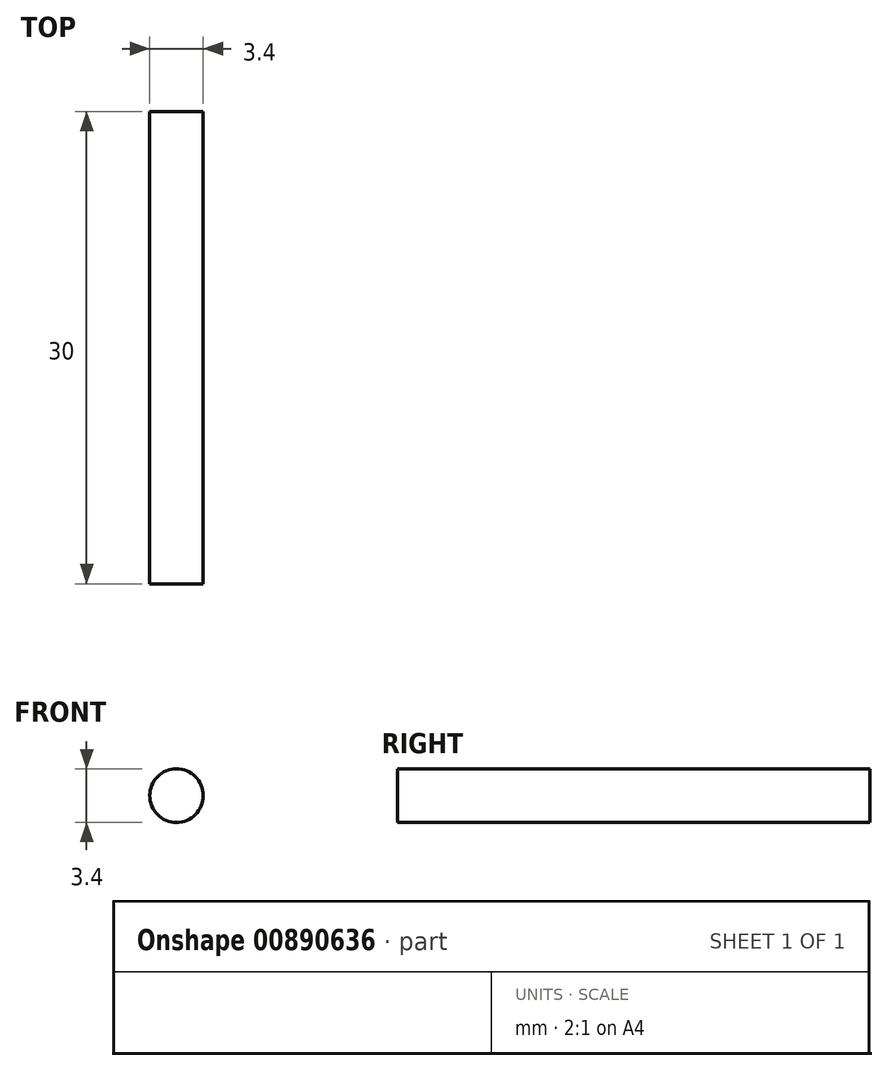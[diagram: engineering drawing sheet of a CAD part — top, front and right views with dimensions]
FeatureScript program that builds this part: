
annotation { "Feature Type Name" : "Feature", "Feature Type Description" : "" }
export const myFeature = defineFeature(function(context is Context, id is Id, definition is map)
    precondition{}
    {
        {
            var Q0;
            Q0=qCreatedBy(makeId("Front.planeOp"),FACE);
            var sketch = newSketch(context, id + "F0", { "sketchPlane" : qUnion([Q0])});
            skCircle(sketch, "E0", {"center": v(0, 0) * mm, "radius": 1.7 * mm});
            skSolve(sketch);
        }
        {
            var Q0;
            Q0=makeQuery(id+"F0.imprint","IMPRINT",FACE,{"disambiguationData":[TD([[makeQuery(id+"F0.imprint","IMPRINT",EDGE,{"derivedFrom":sQuery(id+"F0.wireOp",EDGE,"E0")}),1.0]])]});
            extrude(context, id + "F1", {"entities" : qUnion([Q0]), "depth" : 30 * mm, "offsetDistance" : 25 * mm});
        }
    });
